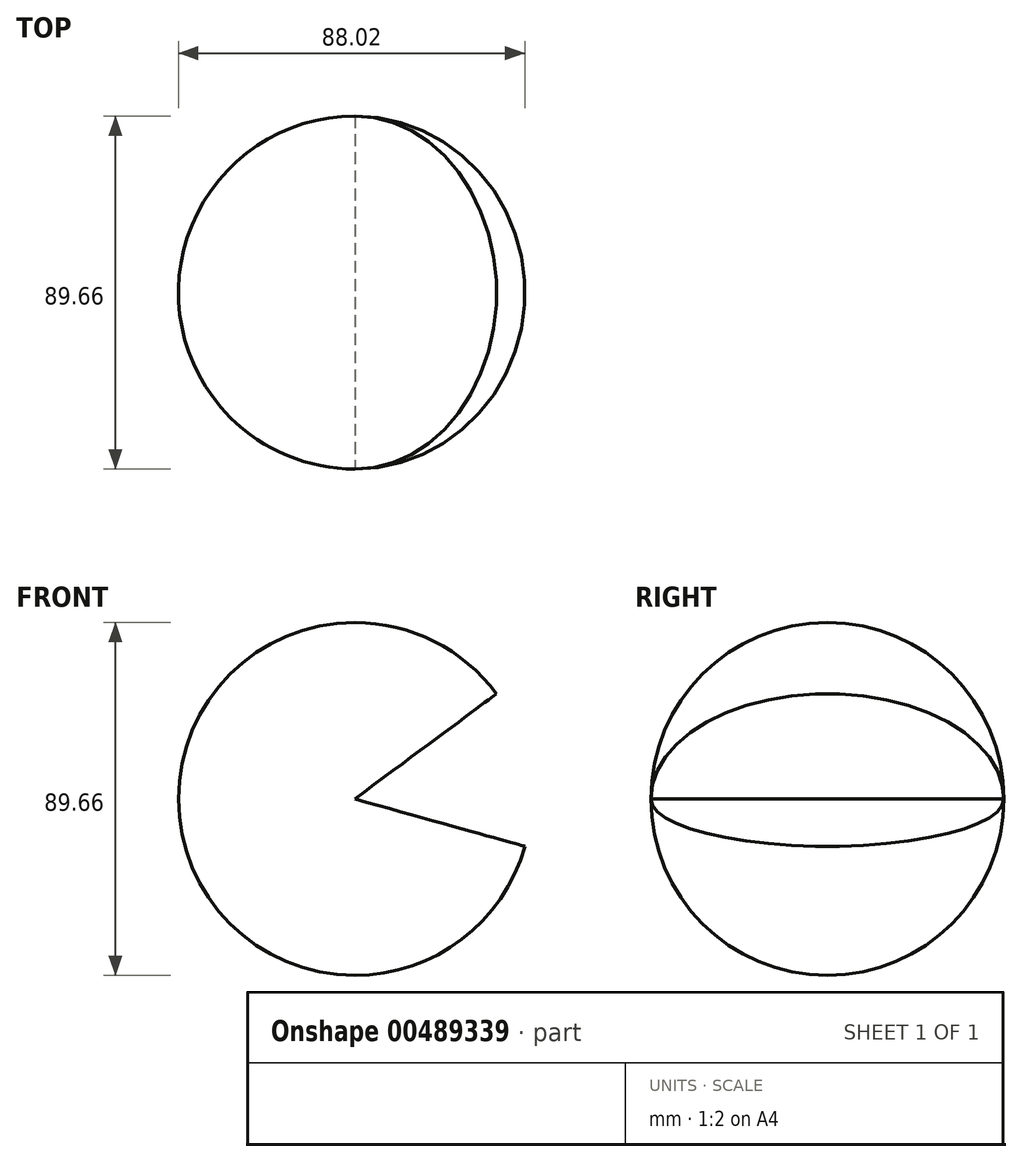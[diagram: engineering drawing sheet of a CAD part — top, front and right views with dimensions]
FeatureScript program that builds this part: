
annotation { "Feature Type Name" : "Feature", "Feature Type Description" : "" }
export const myFeature = defineFeature(function(context is Context, id is Id, definition is map)
    precondition{}
    {
        {
            var Q0;
            Q0=qCreatedBy(makeId("Front.planeOp"),FACE);
            var sketch = newSketch(context, id + "F0", { "sketchPlane" : qUnion([Q0])});
            skCircle(sketch, "E0", {"center": v(0, 0) * mm, "radius": 44.83 * mm});
            skLineSegment(sketch, "E1", {"start": v(0, 51.38) * mm, "end": v(0, -64.1) * mm});
            skSolve(sketch);
        }
        {
            var Q0;
            {var subQ0=sQuery(id+"F0.wireOp",EDGE,"E1");var subQ1=sQuery(id+"F0.wireOp",EDGE,"E0");var subQ2=makeQuery(id+"F0.imprint","INTERSECT",VERTEX,{"disambiguationData":[OD(0.0)],"derivedFrom":[subQ1,subQ0]});Q0=makeQuery(id+"F0.imprint","IMPRINT",FACE,{"disambiguationData":[TD([[makeQuery(id+"F0.imprint","IMPRINT",EDGE,{"disambiguationData":[TD([[subQ2,-1.0]])],"derivedFrom":subQ1}),1.0]])]});}
            var Q1;
            Q1=sQuery(id+"F0.wireOp",EDGE,"E1");
            revolve(context, id + "F1", {"entities" : qUnion([Q0]), "axis" : qUnion([Q1]), "revolveType" : RevolveType.FULL});
        }
        {
            var Q0;
            Q0=qCreatedBy(makeId("Front.planeOp"),FACE);
            var sketch = newSketch(context, id + "F2", { "sketchPlane" : qUnion([Q0])});
            skLineSegment(sketch, "E2", {"start": v(47.27, 35.09) * mm, "end": v(0, 0) * mm});
            skLineSegment(sketch, "E3", {"start": v(0, 0) * mm, "end": v(45.52, -12.68) * mm});
            skLineSegment(sketch, "E4", {"start": v(47.27, 35.09) * mm, "end": v(45.52, -12.68) * mm});
            skSolve(sketch);
        }
        {
            var Q0;
            Q0 = qSketchRegion(id + "F2", true);
            extrude(context, id + "F3", {"entities" : qUnion([Q0]), "operationType" : NewBodyOperationType.REMOVE, "endBound" : BoundingType.SYMMETRIC, "oppositeDirection" : true, "depth" : 101.6 * mm});
        }
    });
